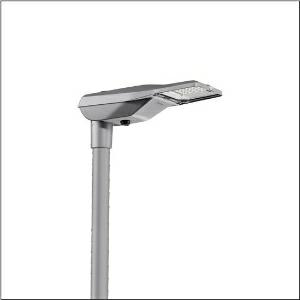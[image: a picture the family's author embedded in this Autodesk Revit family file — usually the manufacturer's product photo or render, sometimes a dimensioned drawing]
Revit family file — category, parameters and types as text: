
# Revit family: streetlight_sl_21_micro___p0_8ab_5xe1r33r08db_894c
name_source: partatom
category: Lighting Fixtures
units: mm (PartAtom-declared; Revit-internal decimal feet)

## family parameters
Cut with Voids When Loaded = No
Host = Face
Light Source = No
Part Type = Normal
Room Calculation Point = No
Round Connector Dimension = Use Diameter
Shared = No

## types (1)
- --- (1 x LED, 4470 lm, 39.1 W, 3000K)
    Apparent Load = 39 VA
    CIE Flux Codes = 36 71 98 100 100
    Color Rendering = 70
    Color Temperature = 3000K
    Default Elevation = 1800 mm
    Description = Streetlight SL 21 micro, mast luminaire, primary light control with lens, of PMMA, primary optical cover: cover, of toughened safety glass, transparent, light distribution: P0.8aB, light emission: direct distribution, primary light characteristic: asymmetric, installation type: post-top, side-entry, LED, High Power LED, rated luminous flux: 4.470lm, luminous efficacy: 114lm/W, light colour: 730, colour temperature: 3000K, control gear: D4i, control: pre-setting: logarithmic dimming characteristic, flexible luminous flux parameterisation, time-dependent luminous flux control, constant luminous flux control, overheat protection, mains connection: 220..240V, AC, 50/60Hz, start of lifetime: 39W, end of service life: 41W, reduction: 18W, luminaire housing, of diecast aluminium, powder-coated, SITECO metallic grey (DB 702S), corrosivity category C5 high according to DIN EN ISO 12944, multi-level sealing system, sealing non-destructively replaceable, inclination adjustable: 0°, 5°, 10°, 15°, please order mast flange separately, length: 528mm, width: 235mm, height: 110mm, mast flange for spigot size: 42mm (side-entry): 5XC10008XM4, 60/48mm (side-entry/post-top): 5XC10108XM2, 76/60mm (side-entry/post-top): 5XC10108XM1, Smart Interface below, protection rating (complete): IP66, insulation class (complete): insulation class II (safety insulation), certification: CE, ENEC, ENEC+, VDE, impact resistance: IK10, permissible operating ambient temperature for outdoor applications: -40..+50°C, standard-compliant lighting for roads and squares, packaging unit: 1 piece

Light Distribution: P0.8aB
    Height = 110 mm
    Lamp = 1 x LED
    Lamp Light Flux = 4470 lm
    Lamp Power = 39.1 W
    Lamp count = 1
    Length = 528 mm
    Luminous efficacy = 114 lm/W
    Manufacturer = Siteco
    ModVariant = No
    Model = 5XE1R33R08DB
    Number of Poles = 1
    OnlyDefault = Yes
    Power Factor = 1
    Product Name = Streetlight SL 21 micro | P0.8aB
    Product group = mast luminaire | pylon top
    ProductGroupID = 6100
    Protection Class = Protection class II
    Protection Degree = IP 66
    RLX_Detail_Level = 1
    RLX_Emergency_Light_Flux = 0 lm
    RLX_Emergency_Type = 0
    RLX_Emergency_Type_DB = No
    RlxData = <blob elided: 98437 chars, md5=33d7f135>
    Socket = socket
    Standby Power = 0 W
    System Light Flux = 4470 lm
    System Power = 39 W
    Type Comments = factory setting: luminous flux: 100 % | dim-lin: 254 | 765 mA
    Type Image = l_1277290.jpg
    URL = http://relux.com
    VarID = @adj_082899
    Voltage = 0 V
    Weight = 0.00 kg
    Width = 235 mm

## geometry (parser evidence)
native form markers: Blend x4, Sweep x11
no freeform markers — native parametric forms only
